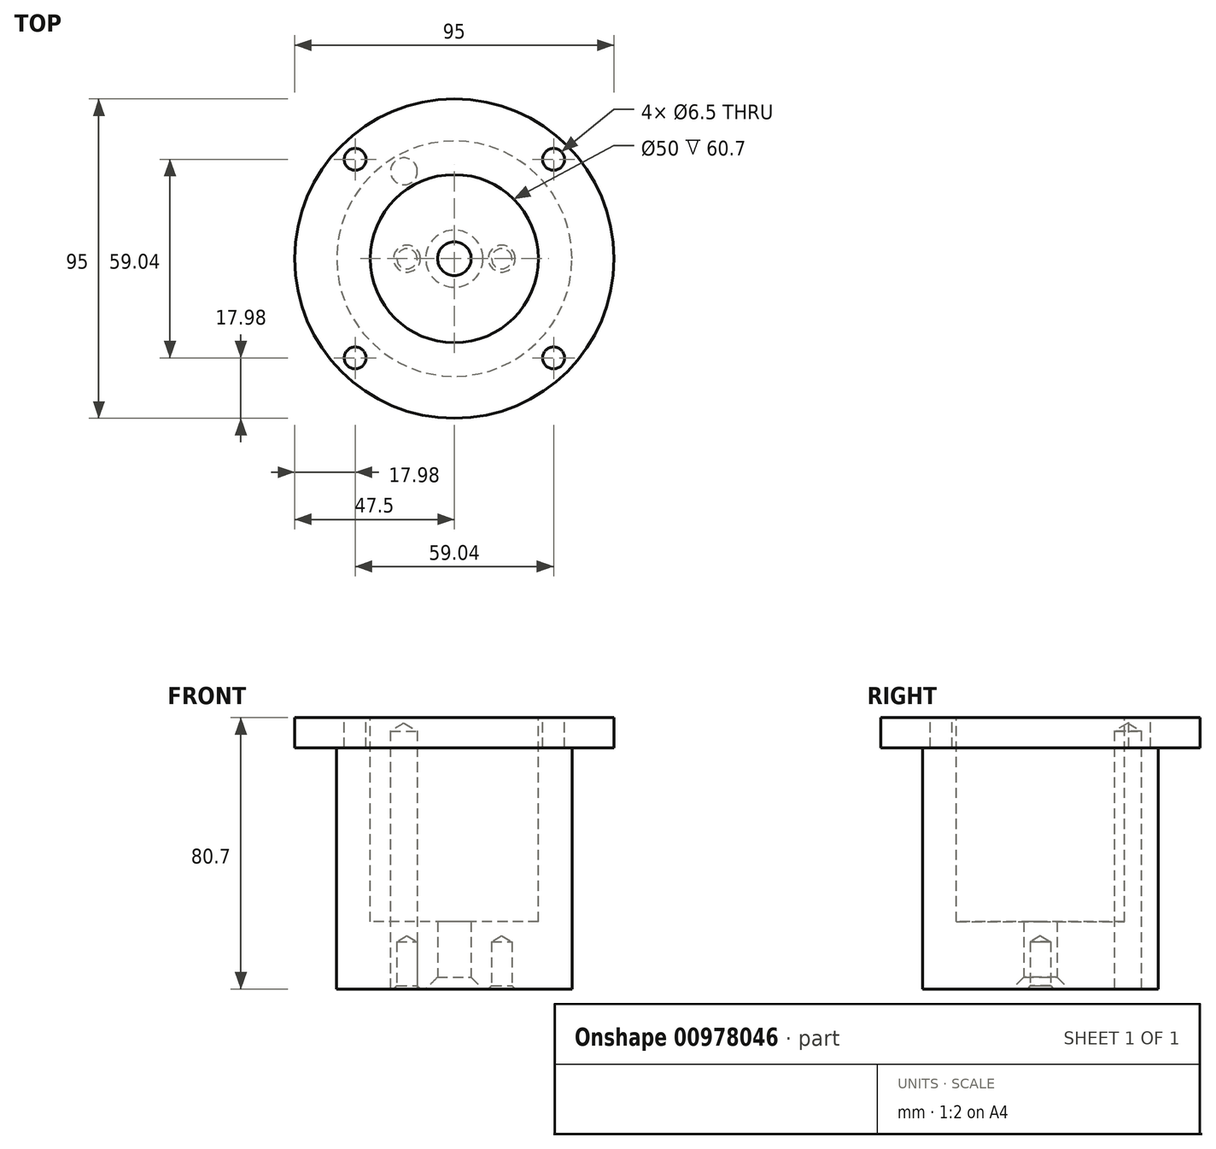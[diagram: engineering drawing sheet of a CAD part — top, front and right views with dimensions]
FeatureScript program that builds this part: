
annotation { "Feature Type Name" : "Feature", "Feature Type Description" : "" }
export const myFeature = defineFeature(function(context is Context, id is Id, definition is map)
    precondition{}
    {
        {
            var Q0;
            Q0=qCreatedBy(makeId("Top.planeOp"),FACE);
            var sketch = newSketch(context, id + "F0", { "sketchPlane" : qUnion([Q0])});
            skCircle(sketch, "E0", {"center": v(0, 0) * mm, "radius": 35 * mm});
            skSolve(sketch);
        }
        {
            var Q0;
            Q0 = qSketchRegion(id + "F0", true);
            extrude(context, id + "F1", {"entities" : qUnion([Q0]), "depth" : 80.7 * mm, "offsetDistance" : 25 * mm});
        }
        {
            var Q0;
            Q0=makeQuery(id+"F1.opExtrude","CAP_FACE",FACE,{"disambiguationData":[OSD([sQuery(id+"F0.wireOp",EDGE,"E0")])],"isStart":false});
            var sketch = newSketch(context, id + "F2", { "sketchPlane" : qUnion([Q0])});
            skCircle(sketch, "E1", {"center": v(0, 0) * mm, "radius": 47.5 * mm});
            skSolve(sketch);
        }
        {
            var Q0;
            Q0 = qSketchRegion(id + "F2", true);
            extrude(context, id + "F3", {"entities" : qUnion([Q0]), "operationType" : NewBodyOperationType.ADD, "oppositeDirection" : true, "depth" : 9 * mm, "offsetDistance" : 25 * mm});
        }
        {
            var Q0;
            Q0=makeQuery(id+"F3.boolean.opBoolean","MERGE",FACE,{"derivedFrom":[makeQuery(id+"F1.opExtrude","CAP_FACE",FACE,{"disambiguationData":[OSD([sQuery(id+"F0.wireOp",EDGE,"E0")])],"isStart":false}),makeQuery(id+"F3.opExtrude","CAP_FACE",FACE,{"disambiguationData":[OSD([sQuery(id+"F2.wireOp",EDGE,"E1")])],"isStart":true})]});
            var sketch = newSketch(context, id + "F4", { "sketchPlane" : qUnion([Q0])});
            skCircle(sketch, "E2", {"center": v(0, 0) * mm, "radius": 25 * mm});
            skSolve(sketch);
        }
        {
            var Q0;
            Q0 = qSketchRegion(id + "F4", true);
            extrude(context, id + "F5", {"entities" : qUnion([Q0]), "operationType" : NewBodyOperationType.REMOVE, "oppositeDirection" : true, "depth" : 60.7 * mm, "offsetDistance" : 25 * mm});
        }
        {
            var Q0;
            Q0=makeQuery(id+"F1.opExtrude","CAP_FACE",FACE,{"disambiguationData":[OSD([sQuery(id+"F0.wireOp",EDGE,"E0")])],"isStart":true});
            var sketch = newSketch(context, id + "F6", { "sketchPlane" : qUnion([Q0])});
            skPoint(sketch, "E3", {"position": v(0, 0) * mm});
            skSolve(sketch);
        }
        {
            var Q0;
            Q0=sQuery(id+"F6.wireOp",VERTEX,"E3");
            var Q1;
            Q1=makeQuery(id+"F1.opExtrude","SWEPT_BODY",BODY,{"disambiguationData":[OSD([sQuery(id+"F0.wireOp",EDGE,"E0")])]});
            hole(context, id + "F7", {"style" : HoleStyle.C_SINK, "endStyle" : HoleEndStyle.THROUGH, "holeDiameter" : 10 * mm, "cSinkDiameter" : 17 * mm, "cSinkAngle" : 90 * degree, "majorDiameter" : 5 * mm, "isTappedThrough" : true, "tappedDepth" : 12 * mm, "tapClearance" : 3, "locations" : qUnion([Q0]), "scope" : qUnion([Q1])});
        }
        {
            var Q0;
            Q0=makeQuery(id+"F3.boolean.opBoolean","MERGE",FACE,{"derivedFrom":[makeQuery(id+"F1.opExtrude","CAP_FACE",FACE,{"disambiguationData":[OSD([sQuery(id+"F0.wireOp",EDGE,"E0")])],"isStart":false}),makeQuery(id+"F3.opExtrude","CAP_FACE",FACE,{"disambiguationData":[OSD([sQuery(id+"F2.wireOp",EDGE,"E1")])],"isStart":true})]});
            var sketch = newSketch(context, id + "F8", { "sketchPlane" : qUnion([Q0])});
            skLineSegment(sketch, "E4.bottom", {"start": v(29.52, 29.52) * mm, "end": v(-29.52, 29.52) * mm, "construction": true});
            skLineSegment(sketch, "E4.top", {"start": v(29.52, -29.52) * mm, "end": v(-29.52, -29.52) * mm, "construction": true});
            skLineSegment(sketch, "E4.left", {"start": v(29.52, 29.52) * mm, "end": v(29.52, -29.52) * mm, "construction": true});
            skLineSegment(sketch, "E4.right", {"start": v(-29.52, 29.52) * mm, "end": v(-29.52, -29.52) * mm, "construction": true});
            skPoint(sketch, "E4.middle", {"position": v(0, 0) * mm});
            skSolve(sketch);
        }
        {
            var Q0;
            Q0=sQuery(id+"F8.wireOp",VERTEX,"E4.top.start");
            var Q1;
            Q1=sQuery(id+"F8.wireOp",VERTEX,"E4.top.end");
            var Q2;
            Q2=sQuery(id+"F8.wireOp",VERTEX,"E4.bottom.end");
            var Q3;
            Q3=sQuery(id+"F8.wireOp",VERTEX,"E4.bottom.start");
            var Q4;
            Q4=makeQuery(id+"F1.opExtrude","SWEPT_BODY",BODY,{"disambiguationData":[OSD([sQuery(id+"F0.wireOp",EDGE,"E0")])]});
            hole(context, id + "F9", {"style" : HoleStyle.SIMPLE, "endStyle" : HoleEndStyle.THROUGH, "holeDiameter" : 6.5 * mm, "majorDiameter" : 5 * mm, "isTappedThrough" : true, "tappedDepth" : 12 * mm, "tapClearance" : 3, "locations" : qUnion([Q0, Q1, Q2, Q3]), "scope" : qUnion([Q4])});
        }
        {
            var Q0;
            Q0=makeQuery(id+"F1.opExtrude","CAP_FACE",FACE,{"disambiguationData":[OSD([sQuery(id+"F0.wireOp",EDGE,"E0")])],"isStart":true});
            var sketch = newSketch(context, id + "F10", { "sketchPlane" : qUnion([Q0])});
            skCircle(sketch, "E5", {"center": v(0, 0) * mm, "radius": 30 * mm});
            skLineSegment(sketch, "E6", {"start": v(0, 0) * mm, "end": v(0, -30) * mm});
            skLineSegment(sketch, "E7", {"start": v(0, 0) * mm, "end": v(-15, -25.98) * mm});
            skSolve(sketch);
        }
        {
            var Q0;
            Q0=sQuery(id+"F10.wireOp",VERTEX,"E7.end");
            var Q1;
            Q1=makeQuery(id+"F1.opExtrude","SWEPT_BODY",BODY,{"disambiguationData":[OSD([sQuery(id+"F0.wireOp",EDGE,"E0")])]});
            hole(context, id + "F11", {"style" : HoleStyle.SIMPLE, "endStyle" : HoleEndStyle.BLIND, "holeDiameter" : 8 * mm, "majorDiameter" : 5 * mm, "holeDepth" : 76.7 * mm, "isTappedThrough" : true, "tappedDepth" : 12 * mm, "tapClearance" : 3, "locations" : qUnion([Q0]), "scope" : qUnion([Q1])});
        }
        {
            var Q0;
            Q0=makeQuery(id+"F1.opExtrude","CAP_FACE",FACE,{"disambiguationData":[OSD([sQuery(id+"F0.wireOp",EDGE,"E0")])],"isStart":true});
            var sketch = newSketch(context, id + "F12", { "sketchPlane" : qUnion([Q0])});
            skLineSegment(sketch, "E8", {"start": v(35, 0) * mm, "end": v(-35, 0) * mm, "construction": true});
            skPoint(sketch, "E9", {"position": v(14.1, 0) * mm});
            skPoint(sketch, "E10", {"position": v(-14.1, 0) * mm});
            skLineSegment(sketch, "E11", {"start": v(0, 0) * mm, "end": v(0, -35) * mm, "construction": true});
            skSolve(sketch);
        }
        {
            var Q0;
            Q0=sQuery(id+"F12.wireOp",VERTEX,"E10");
            var Q1;
            Q1=sQuery(id+"F12.wireOp",VERTEX,"E9");
            var Q2;
            Q2=makeQuery(id+"F1.opExtrude","SWEPT_BODY",BODY,{"disambiguationData":[OSD([sQuery(id+"F0.wireOp",EDGE,"E0")])]});
            hole(context, id + "F13", {"style" : HoleStyle.C_SINK, "endStyle" : HoleEndStyle.BLIND, "holeDiameter" : 6 * mm, "cSinkDiameter" : 8 * mm, "cSinkAngle" : 90 * degree, "majorDiameter" : 4 * mm, "holeDepth" : 14 * mm, "isTappedThrough" : true, "tappedDepth" : 12 * mm, "tapClearance" : 3, "locations" : qUnion([Q0, Q1]), "scope" : qUnion([Q2])});
        }
    });
